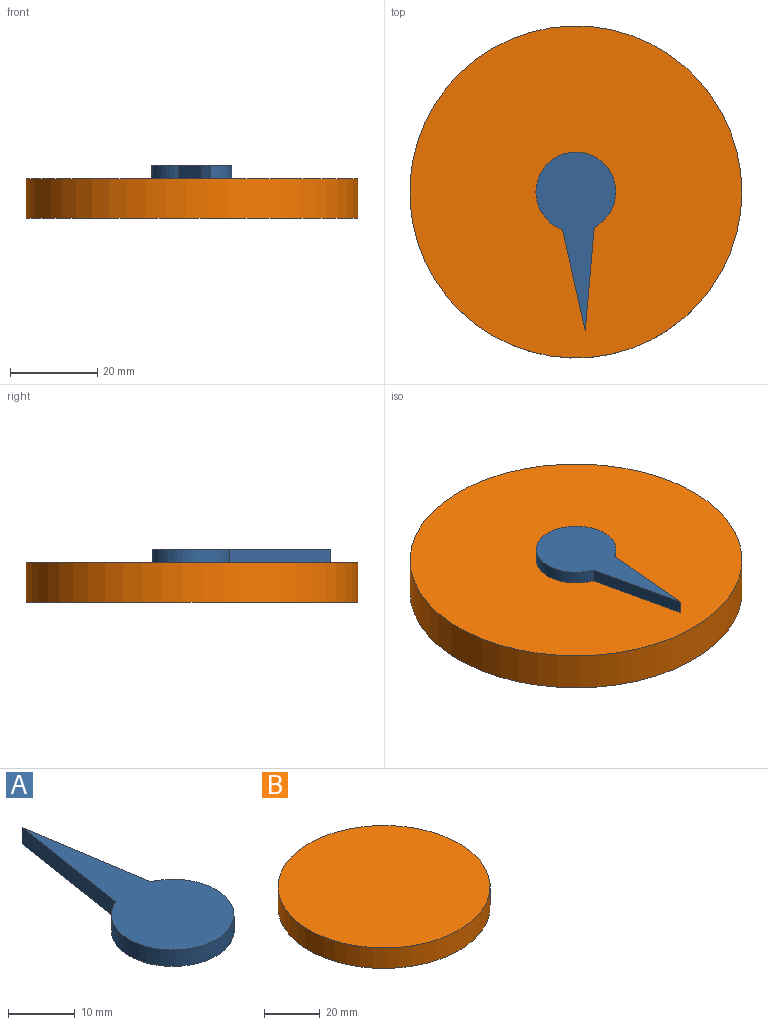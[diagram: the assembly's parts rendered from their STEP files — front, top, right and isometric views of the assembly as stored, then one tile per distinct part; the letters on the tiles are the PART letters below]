
ASSEMBLY  parts=2 mates=1
PART A: 5 faces, bbox 18.3x41x3 mm
  f0: cylinder r=9.16mm len=18.31mm, axis (0,0,-1), area 150mm2, adj f1,f2,f3,f4
  f1: plane 23.47x3.66mm, normal (0.99,0.15,0), area 71.3mm2, adj f0,f2,f3,f4
  f2: plane 23.47x3.66mm, normal (-0.99,0.15,0), area 71.3mm2, adj f0,f1,f3,f4
  f3: plane 41.02x18.31mm, normal (0,0,1), area 345.5mm2, adj f0,f1,f2
  f4: plane 41.02x18.31mm, normal (0,0,-1), area 345.5mm2, adj f0,f1,f2
PART B: 3 faces, bbox 76.2x76.2x9 mm
  f0: cylinder r=38.09mm len=76.17mm, axis (0,0,-1), area 2153.7mm2, adj f1,f2
  f1: plane 76.17x76.17mm, normal (0,0,1), area 4557.1mm2, adj f0
  f2: plane 76.17x76.17mm, normal (0,0,-1), area 4557.1mm2, adj f0
PLACE A rot(axis=(0,0,-1),176.1deg) t=(-6.11,1.85,2.07)mm
PLACE B t=(-6.11,1.85,2.07)mm fixed
MATE revolute B.f0 <-> A.f0  axis (0,0,1) through (-6.11,1.85,11.07)mm
